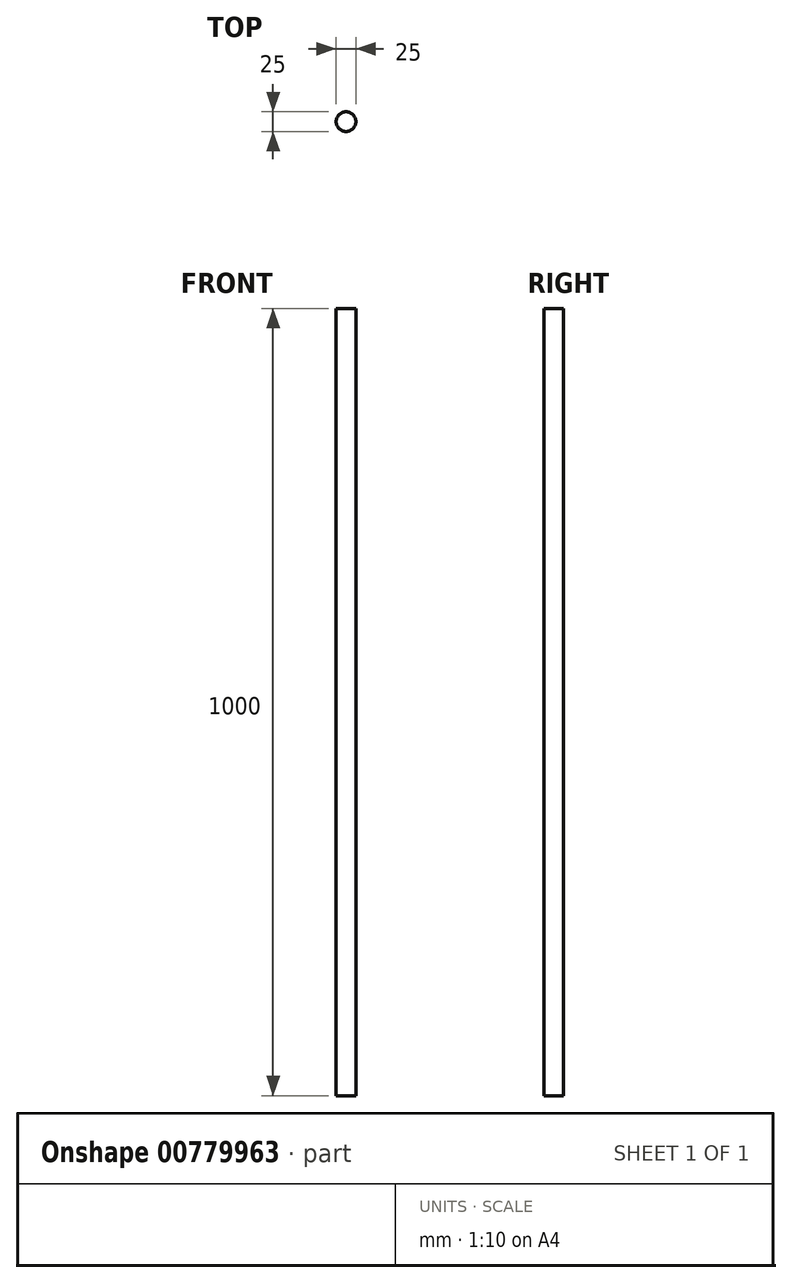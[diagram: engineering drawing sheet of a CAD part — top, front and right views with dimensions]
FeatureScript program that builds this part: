
annotation { "Feature Type Name" : "Feature", "Feature Type Description" : "" }
export const myFeature = defineFeature(function(context is Context, id is Id, definition is map)
    precondition{}
    {
        {
            var Q0;
            Q0=qCreatedBy(makeId("Top.planeOp"),FACE);
            var sketch = newSketch(context, id + "F0", { "sketchPlane" : qUnion([Q0])});
            skCircle(sketch, "E0", {"center": v(0, 0) * mm, "radius": 12.5 * mm});
            skSolve(sketch);
        }
        {
            var Q0;
            Q0=qSketchRegion(id+"F0",true);
            extrude(context, id + "F1", {"entities" : qUnion([Q0]), "depth" : 1000 * mm, "offsetDistance" : 25.4 * mm});
        }
    });
